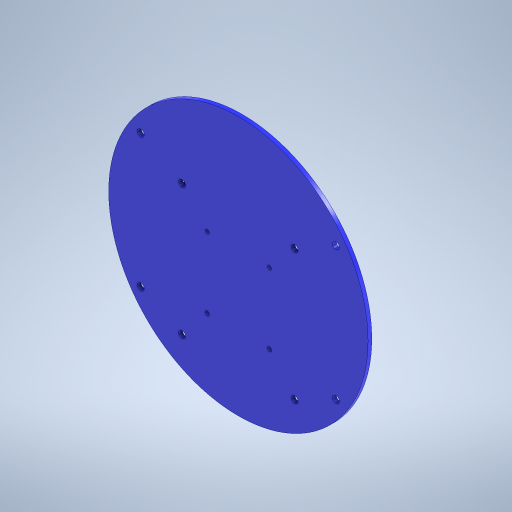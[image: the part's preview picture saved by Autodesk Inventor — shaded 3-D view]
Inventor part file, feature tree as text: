
AUTODESK INVENTOR PART (.ipt)
format: ipt  version: 2023 (Build 270158030, 158C)  size: 333,312 bytes
history: native  units: mm
features: extrude x9, other x7, sketch x3, mirror x3, projected_geometry x1
ambient origin geometry x8: Origin, YZ Plane, XZ Plane, XY Plane, X Axis, Y Axis, Z Axis, Center Point
bodies: Body1 (feature_tree), Body2 (feature_tree), Body3 (feature_tree), Body4 (feature_tree), Body5 (feature_tree), Body6 (feature_tree), Body7 (feature_tree)
feature tree (23):
  other  "PCB_Azul"
  extrude  "Extrusión1"  Depth=1.6mm TaperAngle=0.0deg
  sketch  "Boceto2"  dims[d3=2.9mm d4=28.25mm]
  extrude  "Extrusión2"  Depth=28.25mm
  mirror  "Simetría1"
  mirror  "Simetría2"
  extrude  "Extrusión3"  Depth=5.75mm
  mirror  "Simetría3"
  sketch  "Boceto4"  dims[d5=41.4mm d6=23.875mm d8=12.5mm d9=1.6mm d10=0.0mm d11=1.6mm d12=0.0mm d13=55.5mm d14=1.85mm d15=30.0mm d16=1.7mm d17=13.21mm d18=29.5mm d19=51.1mm d20=5.0mm d21=2.15mm d22=13.35mm d23=0.0mm d24=25.2mm d25=5.11mm d26=5.86mm d27=15.0mm d28=2.5mm d29=33.5mm d30=10.15mm d31=8.4mm d32=43.0mm d33=24.5mm d34=9.8mm d35=4.35mm d36=26.25mm d37=7.5mm d38=12.75mm d39=7.75mm d40=14.5mm d41=6.5mm d42=4.3mm d43=0.0mm d44=4.5mm d45=0.0mm d46=0.85mm d47=0.0mm d48=2.45mm d49=0.0mm d50=6.25mm d51=10.0mm d52=20.0mm d53=5.75mm d54=0.0mm]
  extrude  "Extrusión4"  Depth=12.5mm
  extrude  "Extrusión5"  Depth=1.6mm TaperAngle=0.0deg
  extrude  "Extrusión6"  Depth=1.6mm TaperAngle=0.0deg
  extrude  "Extrusión7"  Depth=5.75mm
  extrude  "Extrusión8"  Depth=1.85mm
  extrude  "Extrusión9"  Depth=5.75mm
  sketch  "Boceto1"  dims[d0=110.0mm d1=1.6mm d2=0.0mm]
  projected_geometry  "Contorno proyectado1"
  other  "HAT_RPI"
  other  "Sólido3"
  other  "Sólido4"
  other  "Sólido5"
  other  "Sólido6"
  other  "Sólido7"
